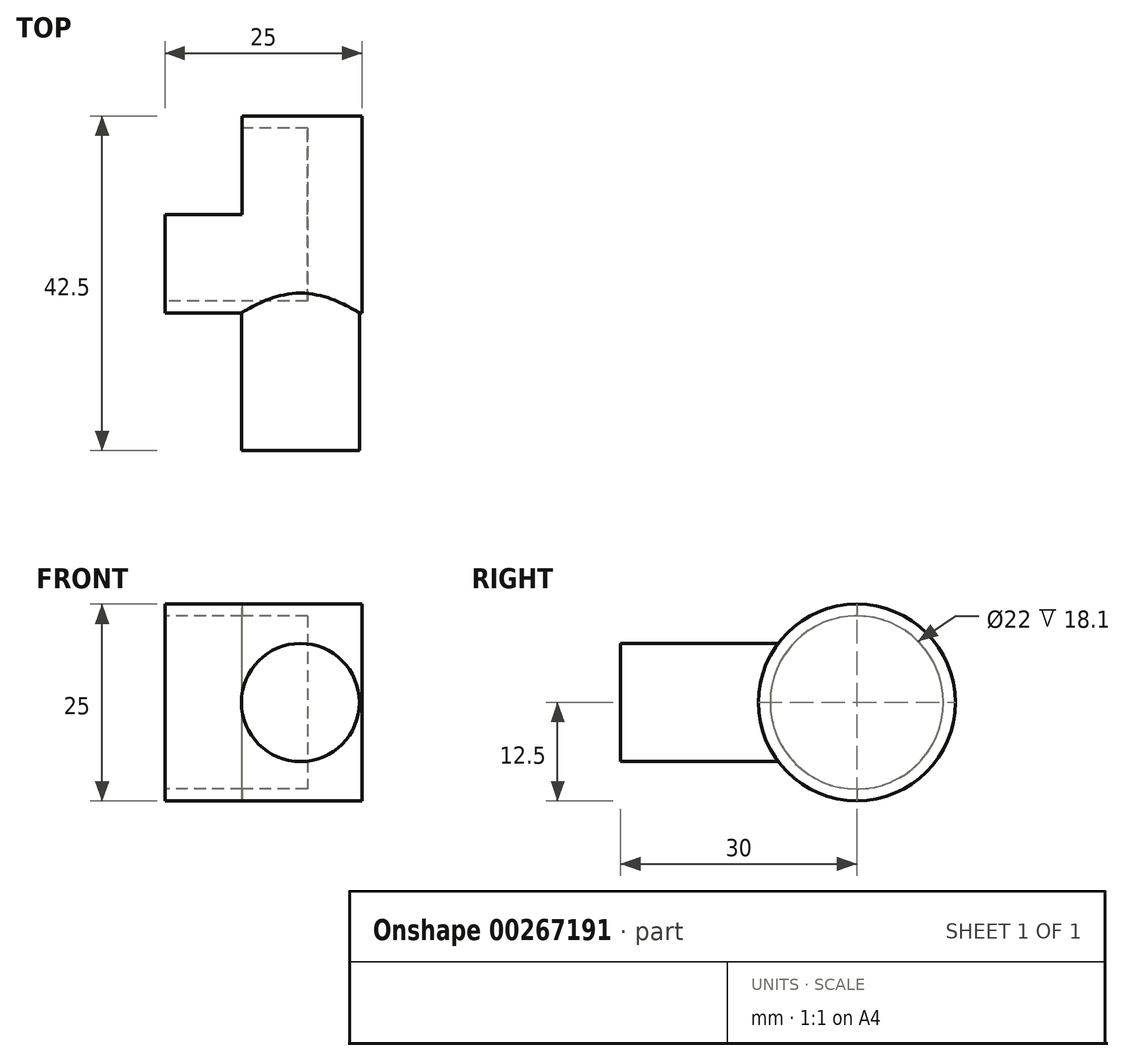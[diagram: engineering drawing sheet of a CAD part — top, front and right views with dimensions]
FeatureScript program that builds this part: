
annotation { "Feature Type Name" : "Feature", "Feature Type Description" : "" }
export const myFeature = defineFeature(function(context is Context, id is Id, definition is map)
    precondition{}
    {
        {
            var Q0;
            Q0=qCreatedBy(makeId("Right.planeOp"),FACE);
            cPlane(context, id + "F0", {"entities" : qUnion([Q0]), "cplaneType" : CPlaneType.OFFSET, "offset" : 7.8 * mm, "width" : 150 * mm, "height" : 150 * mm});
        }
        {
            var Q0;
            Q0=qCreatedBy(makeId("Front.planeOp"),FACE);
            var sketch = newSketch(context, id + "F1", { "sketchPlane" : qUnion([Q0])});
            skCircle(sketch, "E0", {"center": v(0, 0) * mm, "radius": 7.5 * mm});
            skSolve(sketch);
        }
        {
            var Q0;
            Q0=makeQuery(id+"F1.imprint","IMPRINT",FACE,{"disambiguationData":[TD([[makeQuery(id+"F1.imprint","IMPRINT",EDGE,{"derivedFrom":sQuery(id+"F1.wireOp",EDGE,"E0")}),1.0]])]});
            extrude(context, id + "F2", {"entities" : qUnion([Q0]), "depth" : 30 * mm});
        }
        {
            var Q0;
            Q0=qCreatedBy(id+"F0.planeOp",FACE);
            var sketch = newSketch(context, id + "F3", { "sketchPlane" : qUnion([Q0])});
            skCircle(sketch, "E1", {"center": v(0, 0) * mm, "radius": 12.5 * mm});
            skSolve(sketch);
        }
        {
            var Q0;
            Q0=makeQuery(id+"F3.imprint","IMPRINT",FACE,{"disambiguationData":[TD([[makeQuery(id+"F3.imprint","IMPRINT",EDGE,{"derivedFrom":sQuery(id+"F3.wireOp",EDGE,"E1")}),1.0]])]});
            extrude(context, id + "F4", {"entities" : qUnion([Q0]), "operationType" : NewBodyOperationType.ADD, "oppositeDirection" : true, "depth" : 25 * mm});
        }
        {
            var Q0;
            Q0=makeQuery(id+"F4.opExtrude","CAP_FACE",FACE,{"disambiguationData":[OSD([sQuery(id+"F3.wireOp",EDGE,"E1")])],"isStart":false});
            var sketch = newSketch(context, id + "F5", { "sketchPlane" : qUnion([Q0])});
            skCircle(sketch, "E2", {"center": v(0, 0) * mm, "radius": 11 * mm});
            skSolve(sketch);
        }
        {
            var Q0;
            Q0=makeQuery(id+"F5.imprint","IMPRINT",FACE,{"disambiguationData":[TD([[makeQuery(id+"F5.imprint","IMPRINT",EDGE,{"derivedFrom":sQuery(id+"F5.wireOp",EDGE,"E2")}),1.0]])]});
            var Q1;
            Q1=sQuery(id+"F5.wireOp",EDGE,"E2");
            extrude(context, id + "F6", {"entities" : qUnion([Q0]), "operationType" : NewBodyOperationType.REMOVE, "surfaceEntities" : qUnion([Q1]), "oppositeDirection" : true, "depth" : 18.1 * mm});
        }
        {
            var Q0;
            Q0=qCreatedBy(makeId("Right.planeOp"),FACE);
            cPlane(context, id + "F7", {"entities" : qUnion([Q0]), "cplaneType" : CPlaneType.OFFSET, "offset" : 7.4 * mm, "oppositeDirection" : true, "width" : 150 * mm, "height" : 150 * mm});
        }
        {
            var Q0;
            Q0=qCreatedBy(id+"F7.planeOp",FACE);
            var sketch = newSketch(context, id + "F8", { "sketchPlane" : qUnion([Q0])});
            skLineSegment(sketch, "E3.bottom", {"start": v(15, 15.48) * mm, "end": v(0, 15.48) * mm});
            skLineSegment(sketch, "E3.top", {"start": v(15, -15.48) * mm, "end": v(0, -15.48) * mm});
            skLineSegment(sketch, "E3.left", {"start": v(15, 15.48) * mm, "end": v(15, -15.48) * mm});
            skLineSegment(sketch, "E3.right", {"start": v(0, 15.48) * mm, "end": v(0, -15.48) * mm});
            skSolve(sketch);
        }
        {
            var Q0;
            Q0=makeQuery(id+"F8.imprint","IMPRINT",FACE,{"disambiguationData":[TD([[makeQuery(id+"F8.imprint","IMPRINT",EDGE,{"derivedFrom":sQuery(id+"F8.wireOp",EDGE,"E3.bottom")}),1.0]])]});
            extrude(context, id + "F9", {"entities" : qUnion([Q0]), "operationType" : NewBodyOperationType.REMOVE, "oppositeDirection" : true, "depth" : 25 * mm});
        }
    });
